# Revit family: Haworth_MSeries_Storage_TambourDoor_AP_PRELIMINARY
name_source: partatom
category: Furniture Systems
units: mm (PartAtom-declared; Revit-internal decimal feet)

## family parameters
Always vertical = Yes
Cut with Voids When Loaded = No
OmniClass Number = 23.40.70.14.64.21
OmniClass Title = Systems Furniture
Part Type = Normal
Room Calculation Point = No
Round Connector Dimension = Use Diameter
Shared = No
Work Plane-Based = No

## types (4) — shared parameters
Actual Depth = 450 mm  [stored 1.47638 ft]
Assembly Code = E2020200
Bottom Case Offset = 30 mm  [stored 0.0984252 ft]
Case Thickness = 20 mm  [stored 0.0656168 ft]
Description = Haworth - M Series - Storage - Tambour Door
Distance Between Drawer = 2 mm  [stored 0.00656168 ft]
Glide Finish = Haworth _ Polymer _ Black
Lock Finish = Haworth _ Polymer _ Black
Manufacturer = Haworth
Max. Width = 900 mm  [stored 2.95276 ft]
Min. Width = 750 mm  [stored 2.46063 ft]
Model = STMSTXXN
Pull Finish = Haworth _ Paint _ Smooth Plaster
Revision Number = 1
Size = Verify Final Dim. w/ Haworth
Trim Finish = Haworth _ Polymer _ Black
URL = https://www.haworth.com
URL - Product = https://www.haworth.com
Warranty = http://www.haworth.com

## per-type parameters (varying)
| type | Actual Height | Actual Width | Attached 2Hi | Drawer Width | Freestanding 2Hi | Freestanding 3Hi | Freestanding 5Hi | Lock Offset Side | Lock Offset Top | One Drawer | Total Drawer Height | Two Drawer | Width |
| 750w 693h | 693 mm  [stored 2.27362 ft] | 750 mm  [stored 2.46063 ft] | Yes | 680 mm  [stored 2.23097 ft] | No | No | No | 645 mm  [stored 2.11614 ft] | 80 mm  [stored 0.262467 ft] | Yes | 643 mm  [stored 2.10958 ft] | No | 750 mm  [stored 2.46063 ft] |
| 800w 775h | 775 mm  [stored 2.54265 ft] | 800 mm  [stored 2.62467 ft] | No | 730 mm  [stored 2.39501 ft] | Yes | No | No | 695 mm  [stored 2.28018 ft] | 80 mm  [stored 0.262467 ft] | Yes | 725 mm  [stored 2.37861 ft] | No | 800 mm  [stored 2.62467 ft] |
| 900w 1140h | 1140 mm  [stored 3.74016 ft] | 900 mm  [stored 2.95276 ft] | No | 830 mm  [stored 2.7231 ft] | No | Yes | No | 795 mm  [stored 2.60827 ft] | 80 mm  [stored 0.262467 ft] | Yes | 1090 mm  [stored 3.57612 ft] | No | 900 mm  [stored 2.95276 ft] |
| 900w 1800h | 1800 mm  [stored 5.90551 ft] | 900 mm  [stored 2.95276 ft] | No | 410 mm  [stored 1.34514 ft] | No | No | Yes | 375 mm  [stored 1.23031 ft] | 550 mm | No | 1750 mm  [stored 5.74147 ft] | Yes | 900 mm  [stored 2.95276 ft] |

note: [stored X ft] marks values corroborated as IEEE doubles in the binary element streams (Revit-internal decimal feet)

## geometry (parser evidence)
native form markers: Sweep x11
no freeform markers — native parametric forms only
